# Revit family: Faucet-Bath_Filler-KOHLER-LAMINAR-K-14403T_1
name_source: partatom
category: Plumbing Fixtures
revit_build: Autodesk Revit 2017 (Build: 20160225_1515(x64)
units: mm (PartAtom-declared; Revit-internal decimal feet)

## family parameters
Cut with Voids When Loaded = No
Host = Face
OmniClass Number = 23.31.11.00
OmniClass Title = Faucets
Part Type = Normal
Room Calculation Point = No
Round Connector Dimension = Use Diameter
Shared = No

## types (2) — shared parameters
ADA Compliant = No
Assembly Code = D2010
CW Connection = Yes
Cold Water Inlet = Cold Water Inlet
Date Modified = 04/20/2021
Default Elevation = 0"
Drain Included = No
Finish = Kohler-Metal-CP-Polished_Chrome
Flow Rate = 0 GPM
HW Connection = Yes
Height = 37 3/8"
Hot Water Inlet = Hot Water Inlet
Length = 18 1/16"
Manufacturer = KOHLER Co.
Master Format 2014 = 22 41 39
Master Format 2014 Name = Residential Faucets, Supplies, and Trim
Material = Premium Metal Construction
Pressure = 0.00 psi
Product Documentation Link = https://files.kohler.com.cn
Product Name = LAMINAR
Spout Reach = 18 1/16"
URL = http://www.kohler.com.cn
Vent Connection = No
Waste Connection = No
Waste Water Outlet = Waste Water Outlet
WaterSense Certified = No

## per-type parameters (varying)
| type | Cross Handle | Description | Dist | Handle Clearance | Lever Handle | Model | Product Page URL | Type |
| Cross Handle, CP-Polished Chrome | Yes | Floor-standing bathtub faucet bathtub fixed cross handle | 1 3/4" | 1 3/4" | No | K-14403T-3-CP | https://www.kohler.com.cn | 1 |
| Lever Handle, CP-Polished Chrome | No | Floor-standing bathtub faucet bathtub fixed lever handle | 0" | 2 5/8" | Yes | K-14403T-4-CP |  | 2 |

## geometry (parser evidence)
native form markers: Sweep x4
no freeform markers — native parametric forms only
